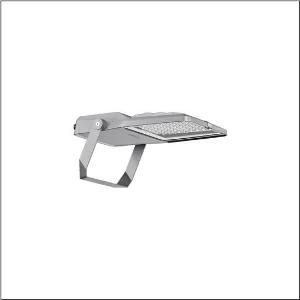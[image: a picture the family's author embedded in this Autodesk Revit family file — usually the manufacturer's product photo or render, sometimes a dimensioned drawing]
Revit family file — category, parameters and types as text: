
# Revit family: floodlight_fl_21_iq_mini___pl64_5xa7771c2e1a_63e9
name_source: partatom
category: Lighting Fixtures
units: mm (PartAtom-declared; Revit-internal decimal feet)

## family parameters
Cut with Voids When Loaded = No
Host = Face
Light Source = No
Part Type = Normal
Room Calculation Point = No
Round Connector Dimension = Use Diameter
Shared = No

## types (1)
- --- (1 x LED, 11790 lm, 87.2 W, 3000K)
    Apparent Load = 87 VA
    CIE Flux Codes = 28 80 98 100 100
    Color Rendering = 70
    Color Temperature = 3000K
    Default Elevation = 1800 mm
    Description = Floodlight FL 21 iQ mini, floodlight, primary light control with lens, of PMMA, primary optical cover: protective disc, of toughened safety glass, transparent, light distribution: PL64, light emission: direct distribution, installation type: surface-mounted, LED, High Power LED, rated luminous flux: 11.790lm, luminous efficacy: 135lm/W, light colour: 730, colour temperature: 3000K, control: Auto-Match, Temp-Guard, Lumen-Switch, Night-Set, Smart-Wire, Light-Fading, Desk-Remote (wireless, voltage-free reading and setting of iQ features in the workshop via application-optimized NFC function/RFID function), optimised constant luminous flux control (CLO 2.0), with terminal, 6-pole, mains connection: 220..240V, AC, 50/60Hz, start of lifetime: 87W, end of service life: 92W, reduction: 40W, luminaire housing, of diecast aluminium, powder-coated, Siteco® metallic grey (DB 702S), corrosivity category C5 mid according to DIN EN ISO 12944, sealing non-destructively replaceable, mounting bracket, of steel, galvanised, powder-coated, Siteco® metallic grey (DB 702S), protection rating (complete): IP66, insulation class (complete): insulation class II (safety insulation), certification: CE, ENEC, VDE, protection symbol: D, impact resistance: IK08, permissible operating ambient temperature: -40..+40°C, permissible operating ambient temperature for outdoor applications: -40..+50°C, standard: DIN EN 12944, LABS conformity tested according to VDMA 24364:2018-05, packaging unit: 1 piece

Light Distribution: PL64
    Height = 70 mm
    Lamp = 1 x LED
    Lamp Light Flux = 11790 lm
    Lamp Power = 87.2 W
    Lamp count = 1
    Length = 485 mm
    Luminous efficacy = 135 lm/W
    Manufacturer = Siteco
    ModVariant = No
    Model = 5XA7771C2E1A
    Number of Poles = 1
    OnlyDefault = Yes
    Power Factor = 1
    Product Name = Floodlight FL 21 iQ mini | PL64
    Product group = floodlight | pylon annexe
    ProductGroupID = 6200
    Protection Class = Protection class II
    Protection Degree = IP 66
    RLX_Detail_Level = 1
    RLX_Emergency_Light_Flux = 0 lm
    RLX_Emergency_Type = 0
    RLX_Emergency_Type_DB = No
    RlxData = <blob elided: 96245 chars, md5=be5012cb>
    Socket = socket
    Standby Power = 0 W
    System Light Flux = 11790 lm
    System Power = 87 W
    Type Comments = factory setting: luminous flux: 100 % | dim-lin: 254 | 456 mA
    Type Image = l_1006845.jpg
    URL = http://relux.com
    VarID = @adj_098985
    Voltage = 0 V
    Weight = 0.00 kg
    Width = 337 mm

## geometry (parser evidence)
native form markers: Blend x4, Sweep x13
no freeform markers — native parametric forms only
